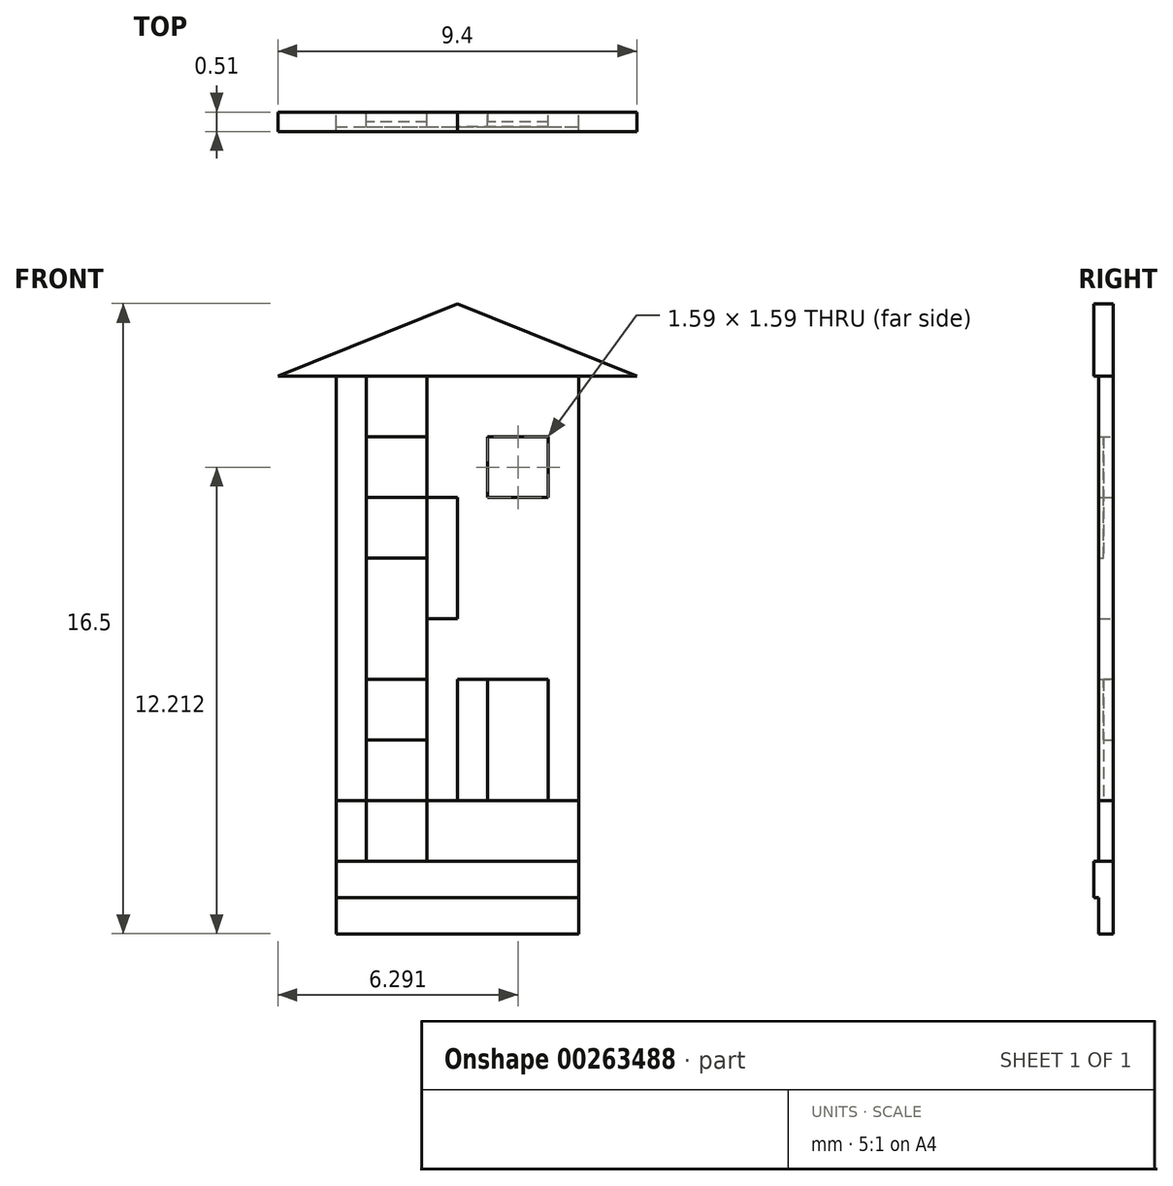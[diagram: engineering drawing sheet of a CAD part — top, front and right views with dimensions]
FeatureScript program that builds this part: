
annotation { "Feature Type Name" : "Feature", "Feature Type Description" : "" }
export const myFeature = defineFeature(function(context is Context, id is Id, definition is map)
    precondition{}
    {
        {
            var Q0;
            Q0=qCreatedBy(makeId("Front.planeOp"),FACE);
            var sketch = newSketch(context, id + "F0", { "sketchPlane" : qUnion([Q0])});
            skLineSegment(sketch, "E0.bottom", {"start": v(-30.22, 33.13) * mm, "end": v(-23.87, 33.13) * mm});
            skLineSegment(sketch, "E0.top", {"start": v(-30.22, 20.43) * mm, "end": v(-23.87, 20.43) * mm});
            skLineSegment(sketch, "E0.left", {"start": v(-30.22, 33.13) * mm, "end": v(-30.22, 20.43) * mm});
            skLineSegment(sketch, "E0.right", {"start": v(-23.87, 33.13) * mm, "end": v(-23.87, 20.43) * mm});
            skLineSegment(sketch, "E1", {"start": v(-27.05, 26.78) * mm, "end": v(-27.05, 20.43) * mm});
            skLineSegment(sketch, "E2", {"start": v(-23.87, 26.78) * mm, "end": v(-30.22, 26.78) * mm});
            skLineSegment(sketch, "E3", {"start": v(-27.05, 33.13) * mm, "end": v(-27.05, 26.78) * mm});
            skLineSegment(sketch, "E4", {"start": v(-28.63, 23.6) * mm, "end": v(-28.63, 20.43) * mm});
            skLineSegment(sketch, "E5", {"start": v(-28.63, 20.43) * mm, "end": v(-28.63, 33.13) * mm});
            skPoint(sketch, "E5.endSnap0", {"position": v(-28.63, 29.96) * mm});
            skLineSegment(sketch, "E6", {"start": v(-25.46, 29.96) * mm, "end": v(-25.46, 33.13) * mm});
            skLineSegment(sketch, "E7", {"start": v(-25.46, 33.13) * mm, "end": v(-25.46, 20.43) * mm});
            skPoint(sketch, "E7.endSnap0", {"position": v(-25.46, 23.6) * mm});
            skLineSegment(sketch, "E8", {"start": v(-28.63, 23.6) * mm, "end": v(-30.22, 23.6) * mm});
            skLineSegment(sketch, "E9", {"start": v(-30.22, 23.6) * mm, "end": v(-23.87, 23.6) * mm});
            skLineSegment(sketch, "E10", {"start": v(-28.63, 29.96) * mm, "end": v(-30.22, 29.96) * mm});
            skLineSegment(sketch, "E11", {"start": v(-30.22, 29.96) * mm, "end": v(-23.87, 29.96) * mm});
            skLineSegment(sketch, "E12", {"start": v(-27.05, 23.6) * mm, "end": v(-27.05, 29.96) * mm});
            skLineSegment(sketch, "E13", {"start": v(-29.43, 31.55) * mm, "end": v(-29.43, 33.13) * mm});
            skLineSegment(sketch, "E14", {"start": v(-29.43, 33.13) * mm, "end": v(-29.43, 20.43) * mm});
            skLineSegment(sketch, "E15", {"start": v(-29.43, 31.55) * mm, "end": v(-30.22, 31.55) * mm});
            skLineSegment(sketch, "E16", {"start": v(-30.22, 31.55) * mm, "end": v(-23.87, 31.55) * mm});
            skLineSegment(sketch, "E17", {"start": v(-27.84, 28.37) * mm, "end": v(-27.84, 33.13) * mm});
            skLineSegment(sketch, "E18", {"start": v(-27.84, 33.13) * mm, "end": v(-27.84, 20.43) * mm});
            skLineSegment(sketch, "E19", {"start": v(-27.84, 28.37) * mm, "end": v(-30.22, 28.37) * mm});
            skLineSegment(sketch, "E20", {"start": v(-30.22, 28.37) * mm, "end": v(-23.87, 28.37) * mm});
            skLineSegment(sketch, "E21", {"start": v(-26.25, 25.2) * mm, "end": v(-26.25, 20.43) * mm});
            skLineSegment(sketch, "E22", {"start": v(-26.25, 20.43) * mm, "end": v(-26.25, 33.13) * mm});
            skLineSegment(sketch, "E23", {"start": v(-26.25, 25.2) * mm, "end": v(-23.87, 25.2) * mm});
            skLineSegment(sketch, "E24", {"start": v(-23.87, 25.2) * mm, "end": v(-30.22, 25.2) * mm});
            skLineSegment(sketch, "E25", {"start": v(-24.67, 22.02) * mm, "end": v(-24.67, 33.13) * mm});
            skLineSegment(sketch, "E26", {"start": v(-24.67, 33.13) * mm, "end": v(-24.67, 20.43) * mm});
            skLineSegment(sketch, "E27", {"start": v(-24.67, 22.02) * mm, "end": v(-23.87, 22.02) * mm});
            skLineSegment(sketch, "E28", {"start": v(-23.87, 22.02) * mm, "end": v(-30.22, 22.02) * mm});
            skPoint(sketch, "E28.endSnap0", {"position": v(-28.63, 22.02) * mm});
            skLineSegment(sketch, "E29", {"start": v(-30.22, 33.13) * mm, "end": v(-31.75, 33.13) * mm});
            skLineSegment(sketch, "E30", {"start": v(-23.87, 33.13) * mm, "end": v(-22.35, 33.13) * mm});
            skLineSegment(sketch, "E31", {"start": v(-27.05, 33.13) * mm, "end": v(-27.05, 35.04) * mm});
            skLineSegment(sketch, "E32", {"start": v(-27.05, 35.04) * mm, "end": v(-31.75, 33.13) * mm});
            skLineSegment(sketch, "E33", {"start": v(-27.05, 35.04) * mm, "end": v(-22.35, 33.13) * mm});
            skLineSegment(sketch, "E34.top", {"start": v(-30.22, 18.54) * mm, "end": v(-23.87, 18.54) * mm});
            skLineSegment(sketch, "E34.left", {"start": v(-30.22, 20.43) * mm, "end": v(-30.22, 18.54) * mm});
            skLineSegment(sketch, "E34.right", {"start": v(-23.87, 20.43) * mm, "end": v(-23.87, 18.54) * mm});
            skLineSegment(sketch, "E35.top", {"start": v(-30.22, 19.48) * mm, "end": v(-23.87, 19.48) * mm});
            skLineSegment(sketch, "E35.left", {"start": v(-30.22, 20.43) * mm, "end": v(-30.22, 19.48) * mm});
            skLineSegment(sketch, "E35.right", {"start": v(-23.87, 20.43) * mm, "end": v(-23.87, 19.48) * mm});
            skSolve(sketch);
        }
        {
            var Q0;
            {var subQ0=sQuery(id+"F0.wireOp",EDGE,"E0.left");var subQ1=sQuery(id+"F0.wireOp",EDGE,"E0.bottom");var subQ2=makeQuery(id+"F0.imprint","INTERSECT",VERTEX,{"derivedFrom":[subQ1,subQ0]});Q0=makeQuery(id+"F0.imprint","IMPRINT",FACE,{"disambiguationData":[TD([[makeQuery(id+"F0.imprint","IMPRINT",EDGE,{"disambiguationData":[TD([[subQ2,-1.0]])],"derivedFrom":subQ1}),-1.0]])]});}
            var Q1;
            {var subQ0=sQuery(id+"F0.wireOp",EDGE,"E11");var subQ1=sQuery(id+"F0.wireOp",EDGE,"E0.left");var subQ2=makeQuery(id+"F0.imprint","INTERSECT",VERTEX,{"derivedFrom":[subQ1,subQ0]});Q1=makeQuery(id+"F0.imprint","IMPRINT",FACE,{"disambiguationData":[TD([[makeQuery(id+"F0.imprint","IMPRINT",EDGE,{"disambiguationData":[TD([[subQ2,1.0]])],"derivedFrom":subQ1}),1.0]])]});}
            var Q2;
            {var subQ0=sQuery(id+"F0.wireOp",EDGE,"E11");var subQ1=sQuery(id+"F0.wireOp",EDGE,"E0.left");var subQ2=makeQuery(id+"F0.imprint","INTERSECT",VERTEX,{"derivedFrom":[subQ1,subQ0]});Q2=makeQuery(id+"F0.imprint","IMPRINT",FACE,{"disambiguationData":[TD([[makeQuery(id+"F0.imprint","IMPRINT",EDGE,{"disambiguationData":[TD([[subQ2,-1.0]])],"derivedFrom":subQ1}),1.0]])]});}
            var Q3;
            {var subQ0=sQuery(id+"F0.wireOp",EDGE,"E2");var subQ1=sQuery(id+"F0.wireOp",EDGE,"E0.left");var subQ2=makeQuery(id+"F0.imprint","INTERSECT",VERTEX,{"derivedFrom":[subQ1,subQ0]});Q3=makeQuery(id+"F0.imprint","IMPRINT",FACE,{"disambiguationData":[TD([[makeQuery(id+"F0.imprint","IMPRINT",EDGE,{"disambiguationData":[TD([[subQ2,1.0]])],"derivedFrom":subQ1}),1.0]])]});}
            var Q4;
            {var subQ0=sQuery(id+"F0.wireOp",EDGE,"E2");var subQ1=sQuery(id+"F0.wireOp",EDGE,"E0.left");var subQ2=makeQuery(id+"F0.imprint","INTERSECT",VERTEX,{"derivedFrom":[subQ1,subQ0]});Q4=makeQuery(id+"F0.imprint","IMPRINT",FACE,{"disambiguationData":[TD([[makeQuery(id+"F0.imprint","IMPRINT",EDGE,{"disambiguationData":[TD([[subQ2,-1.0]])],"derivedFrom":subQ1}),1.0]])]});}
            var Q5;
            {var subQ0=sQuery(id+"F0.wireOp",EDGE,"E9");var subQ1=sQuery(id+"F0.wireOp",EDGE,"E0.left");var subQ2=makeQuery(id+"F0.imprint","INTERSECT",VERTEX,{"derivedFrom":[subQ1,subQ0]});Q5=makeQuery(id+"F0.imprint","IMPRINT",FACE,{"disambiguationData":[TD([[makeQuery(id+"F0.imprint","IMPRINT",EDGE,{"disambiguationData":[TD([[subQ2,1.0]])],"derivedFrom":subQ1}),1.0]])]});}
            var Q6;
            {var subQ0=sQuery(id+"F0.wireOp",EDGE,"E9");var subQ1=sQuery(id+"F0.wireOp",EDGE,"E0.left");var subQ2=makeQuery(id+"F0.imprint","INTERSECT",VERTEX,{"derivedFrom":[subQ1,subQ0]});Q6=makeQuery(id+"F0.imprint","IMPRINT",FACE,{"disambiguationData":[TD([[makeQuery(id+"F0.imprint","IMPRINT",EDGE,{"disambiguationData":[TD([[subQ2,-1.0]])],"derivedFrom":subQ1}),1.0]])]});}
            var Q7;
            {var subQ0=sQuery(id+"F0.wireOp",EDGE,"E0.left");var subQ1=sQuery(id+"F0.wireOp",EDGE,"E0.top");var subQ2=makeQuery(id+"F0.imprint","INTERSECT",VERTEX,{"derivedFrom":[subQ1,subQ0]});Q7=makeQuery(id+"F0.imprint","IMPRINT",FACE,{"disambiguationData":[TD([[makeQuery(id+"F0.imprint","IMPRINT",EDGE,{"disambiguationData":[TD([[subQ2,-1.0]])],"derivedFrom":subQ1}),1.0]])]});}
            var Q8;
            {var subQ0=sQuery(id+"F0.wireOp",EDGE,"E5");var subQ1=sQuery(id+"F0.wireOp",EDGE,"E0.top");var subQ2=makeQuery(id+"F0.imprint","INTERSECT",VERTEX,{"derivedFrom":[subQ1,subQ0]});Q8=makeQuery(id+"F0.imprint","IMPRINT",FACE,{"disambiguationData":[TD([[makeQuery(id+"F0.imprint","IMPRINT",EDGE,{"disambiguationData":[TD([[subQ2,-1.0]])],"derivedFrom":subQ1}),1.0]])]});}
            var Q9;
            {var subQ0=sQuery(id+"F0.wireOp",EDGE,"E5");var subQ1=sQuery(id+"F0.wireOp",EDGE,"E0.top");var subQ2=makeQuery(id+"F0.imprint","INTERSECT",VERTEX,{"derivedFrom":[subQ1,subQ0]});Q9=makeQuery(id+"F0.imprint","IMPRINT",FACE,{"disambiguationData":[TD([[makeQuery(id+"F0.imprint","IMPRINT",EDGE,{"disambiguationData":[TD([[subQ2,1.0]])],"derivedFrom":subQ1}),1.0]])]});}
            var Q10;
            {var subQ0=sQuery(id+"F0.wireOp",EDGE,"E1");var subQ1=sQuery(id+"F0.wireOp",EDGE,"E0.top");var subQ2=makeQuery(id+"F0.imprint","INTERSECT",VERTEX,{"derivedFrom":[subQ1,subQ0]});Q10=makeQuery(id+"F0.imprint","IMPRINT",FACE,{"disambiguationData":[TD([[makeQuery(id+"F0.imprint","IMPRINT",EDGE,{"disambiguationData":[TD([[subQ2,1.0]])],"derivedFrom":subQ1}),1.0]])]});}
            var Q11;
            {var subQ0=sQuery(id+"F0.wireOp",EDGE,"E1");var subQ1=sQuery(id+"F0.wireOp",EDGE,"E0.top");var subQ2=makeQuery(id+"F0.imprint","INTERSECT",VERTEX,{"derivedFrom":[subQ1,subQ0]});Q11=makeQuery(id+"F0.imprint","IMPRINT",FACE,{"disambiguationData":[TD([[makeQuery(id+"F0.imprint","IMPRINT",EDGE,{"disambiguationData":[TD([[subQ2,-1.0]])],"derivedFrom":subQ1}),1.0]])]});}
            var Q12;
            {var subQ0=sQuery(id+"F0.wireOp",EDGE,"E7");var subQ1=sQuery(id+"F0.wireOp",EDGE,"E0.top");var subQ2=makeQuery(id+"F0.imprint","INTERSECT",VERTEX,{"derivedFrom":[subQ1,subQ0]});Q12=makeQuery(id+"F0.imprint","IMPRINT",FACE,{"disambiguationData":[TD([[makeQuery(id+"F0.imprint","IMPRINT",EDGE,{"disambiguationData":[TD([[subQ2,1.0]])],"derivedFrom":subQ1}),1.0]])]});}
            var Q13;
            {var subQ0=sQuery(id+"F0.wireOp",EDGE,"E7");var subQ1=sQuery(id+"F0.wireOp",EDGE,"E0.top");var subQ2=makeQuery(id+"F0.imprint","INTERSECT",VERTEX,{"derivedFrom":[subQ1,subQ0]});Q13=makeQuery(id+"F0.imprint","IMPRINT",FACE,{"disambiguationData":[TD([[makeQuery(id+"F0.imprint","IMPRINT",EDGE,{"disambiguationData":[TD([[subQ2,-1.0]])],"derivedFrom":subQ1}),1.0]])]});}
            var Q14;
            {var subQ0=sQuery(id+"F0.wireOp",EDGE,"E0.right");var subQ1=sQuery(id+"F0.wireOp",EDGE,"E0.top");var subQ2=makeQuery(id+"F0.imprint","INTERSECT",VERTEX,{"derivedFrom":[subQ1,subQ0]});Q14=makeQuery(id+"F0.imprint","IMPRINT",FACE,{"disambiguationData":[TD([[makeQuery(id+"F0.imprint","IMPRINT",EDGE,{"disambiguationData":[TD([[subQ2,1.0]])],"derivedFrom":subQ1}),1.0]])]});}
            var Q15;
            {var subQ0=sQuery(id+"F0.wireOp",EDGE,"E9");var subQ1=sQuery(id+"F0.wireOp",EDGE,"E0.right");var subQ2=makeQuery(id+"F0.imprint","INTERSECT",VERTEX,{"derivedFrom":[subQ1,subQ0]});Q15=makeQuery(id+"F0.imprint","IMPRINT",FACE,{"disambiguationData":[TD([[makeQuery(id+"F0.imprint","IMPRINT",EDGE,{"disambiguationData":[TD([[subQ2,-1.0]])],"derivedFrom":subQ1}),-1.0]])]});}
            var Q16;
            {var subQ0=sQuery(id+"F0.wireOp",EDGE,"E9");var subQ1=sQuery(id+"F0.wireOp",EDGE,"E0.right");var subQ2=makeQuery(id+"F0.imprint","INTERSECT",VERTEX,{"derivedFrom":[subQ1,subQ0]});Q16=makeQuery(id+"F0.imprint","IMPRINT",FACE,{"disambiguationData":[TD([[makeQuery(id+"F0.imprint","IMPRINT",EDGE,{"disambiguationData":[TD([[subQ2,1.0]])],"derivedFrom":subQ1}),-1.0]])]});}
            var Q17;
            {var subQ0=sQuery(id+"F0.wireOp",EDGE,"E2");var subQ1=sQuery(id+"F0.wireOp",EDGE,"E0.right");var subQ2=makeQuery(id+"F0.imprint","INTERSECT",VERTEX,{"derivedFrom":[subQ1,subQ0]});Q17=makeQuery(id+"F0.imprint","IMPRINT",FACE,{"disambiguationData":[TD([[makeQuery(id+"F0.imprint","IMPRINT",EDGE,{"disambiguationData":[TD([[subQ2,-1.0]])],"derivedFrom":subQ1}),-1.0]])]});}
            var Q18;
            {var subQ0=sQuery(id+"F0.wireOp",EDGE,"E2");var subQ1=sQuery(id+"F0.wireOp",EDGE,"E0.right");var subQ2=makeQuery(id+"F0.imprint","INTERSECT",VERTEX,{"derivedFrom":[subQ1,subQ0]});Q18=makeQuery(id+"F0.imprint","IMPRINT",FACE,{"disambiguationData":[TD([[makeQuery(id+"F0.imprint","IMPRINT",EDGE,{"disambiguationData":[TD([[subQ2,1.0]])],"derivedFrom":subQ1}),-1.0]])]});}
            var Q19;
            {var subQ0=sQuery(id+"F0.wireOp",EDGE,"E11");var subQ1=sQuery(id+"F0.wireOp",EDGE,"E0.right");var subQ2=makeQuery(id+"F0.imprint","INTERSECT",VERTEX,{"derivedFrom":[subQ1,subQ0]});Q19=makeQuery(id+"F0.imprint","IMPRINT",FACE,{"disambiguationData":[TD([[makeQuery(id+"F0.imprint","IMPRINT",EDGE,{"disambiguationData":[TD([[subQ2,-1.0]])],"derivedFrom":subQ1}),-1.0]])]});}
            var Q20;
            {var subQ0=sQuery(id+"F0.wireOp",EDGE,"E11");var subQ1=sQuery(id+"F0.wireOp",EDGE,"E0.right");var subQ2=makeQuery(id+"F0.imprint","INTERSECT",VERTEX,{"derivedFrom":[subQ1,subQ0]});Q20=makeQuery(id+"F0.imprint","IMPRINT",FACE,{"disambiguationData":[TD([[makeQuery(id+"F0.imprint","IMPRINT",EDGE,{"disambiguationData":[TD([[subQ2,1.0]])],"derivedFrom":subQ1}),-1.0]])]});}
            var Q21;
            {var subQ0=sQuery(id+"F0.wireOp",EDGE,"E0.right");var subQ1=sQuery(id+"F0.wireOp",EDGE,"E0.bottom");var subQ2=makeQuery(id+"F0.imprint","INTERSECT",VERTEX,{"derivedFrom":[subQ1,subQ0]});Q21=makeQuery(id+"F0.imprint","IMPRINT",FACE,{"disambiguationData":[TD([[makeQuery(id+"F0.imprint","IMPRINT",EDGE,{"disambiguationData":[TD([[subQ2,1.0]])],"derivedFrom":subQ1}),-1.0]])]});}
            var Q22;
            {var subQ0=sQuery(id+"F0.wireOp",EDGE,"E7");var subQ1=sQuery(id+"F0.wireOp",EDGE,"E0.bottom");var subQ2=makeQuery(id+"F0.imprint","INTERSECT",VERTEX,{"derivedFrom":[subQ1,subQ0]});Q22=makeQuery(id+"F0.imprint","IMPRINT",FACE,{"disambiguationData":[TD([[makeQuery(id+"F0.imprint","IMPRINT",EDGE,{"disambiguationData":[TD([[subQ2,-1.0]])],"derivedFrom":subQ1}),-1.0]])]});}
            var Q23;
            {var subQ0=sQuery(id+"F0.wireOp",EDGE,"E7");var subQ1=sQuery(id+"F0.wireOp",EDGE,"E0.bottom");var subQ2=makeQuery(id+"F0.imprint","INTERSECT",VERTEX,{"derivedFrom":[subQ1,subQ0]});Q23=makeQuery(id+"F0.imprint","IMPRINT",FACE,{"disambiguationData":[TD([[makeQuery(id+"F0.imprint","IMPRINT",EDGE,{"disambiguationData":[TD([[subQ2,1.0]])],"derivedFrom":subQ1}),-1.0]])]});}
            var Q24;
            {var subQ0=sQuery(id+"F0.wireOp",EDGE,"E3");var subQ1=sQuery(id+"F0.wireOp",EDGE,"E0.bottom");var subQ2=makeQuery(id+"F0.imprint","INTERSECT",VERTEX,{"derivedFrom":[subQ1,subQ0]});Q24=makeQuery(id+"F0.imprint","IMPRINT",FACE,{"disambiguationData":[TD([[makeQuery(id+"F0.imprint","IMPRINT",EDGE,{"disambiguationData":[TD([[subQ2,-1.0]])],"derivedFrom":subQ1}),-1.0]])]});}
            var Q25;
            {var subQ0=sQuery(id+"F0.wireOp",EDGE,"E3");var subQ1=sQuery(id+"F0.wireOp",EDGE,"E0.bottom");var subQ2=makeQuery(id+"F0.imprint","INTERSECT",VERTEX,{"derivedFrom":[subQ1,subQ0]});Q25=makeQuery(id+"F0.imprint","IMPRINT",FACE,{"disambiguationData":[TD([[makeQuery(id+"F0.imprint","IMPRINT",EDGE,{"disambiguationData":[TD([[subQ2,1.0]])],"derivedFrom":subQ1}),-1.0]])]});}
            var Q26;
            {var subQ0=sQuery(id+"F0.wireOp",EDGE,"E5");var subQ1=sQuery(id+"F0.wireOp",EDGE,"E0.bottom");var subQ2=makeQuery(id+"F0.imprint","INTERSECT",VERTEX,{"derivedFrom":[subQ1,subQ0]});Q26=makeQuery(id+"F0.imprint","IMPRINT",FACE,{"disambiguationData":[TD([[makeQuery(id+"F0.imprint","IMPRINT",EDGE,{"disambiguationData":[TD([[subQ2,-1.0]])],"derivedFrom":subQ1}),-1.0]])]});}
            var Q27;
            {var subQ0=sQuery(id+"F0.wireOp",EDGE,"E5");var subQ1=sQuery(id+"F0.wireOp",EDGE,"E0.bottom");var subQ2=makeQuery(id+"F0.imprint","INTERSECT",VERTEX,{"derivedFrom":[subQ1,subQ0]});Q27=makeQuery(id+"F0.imprint","IMPRINT",FACE,{"disambiguationData":[TD([[makeQuery(id+"F0.imprint","IMPRINT",EDGE,{"disambiguationData":[TD([[subQ2,1.0]])],"derivedFrom":subQ1}),-1.0]])]});}
            var Q28;
            {var subQ1=sQuery(id+"F0.wireOp",EDGE,"E3");var subQ3=sQuery(id+"F0.wireOp",EDGE,"E16");var subQ4=makeQuery(id+"F0.imprint","INTERSECT",VERTEX,{"derivedFrom":[subQ1,subQ3]});Q28=makeQuery(id+"F0.imprint","IMPRINT",FACE,{"disambiguationData":[TD([[makeQuery(id+"F0.imprint","IMPRINT",EDGE,{"disambiguationData":[TD([[subQ4,1.0]])],"derivedFrom":subQ3}),-1.0]])]});}
            var Q29;
            {var subQ1=sQuery(id+"F0.wireOp",EDGE,"E3");var subQ3=sQuery(id+"F0.wireOp",EDGE,"E16");var subQ4=makeQuery(id+"F0.imprint","INTERSECT",VERTEX,{"derivedFrom":[subQ1,subQ3]});Q29=makeQuery(id+"F0.imprint","IMPRINT",FACE,{"disambiguationData":[TD([[makeQuery(id+"F0.imprint","IMPRINT",EDGE,{"disambiguationData":[TD([[subQ4,-1.0]])],"derivedFrom":subQ3}),-1.0]])]});}
            var Q30;
            {var subQ0=sQuery(id+"F0.wireOp",EDGE,"E12");var subQ5=sQuery(id+"F0.wireOp",EDGE,"E20");var subQ6=makeQuery(id+"F0.imprint","INTERSECT",VERTEX,{"derivedFrom":[subQ0,subQ5]});Q30=makeQuery(id+"F0.imprint","IMPRINT",FACE,{"disambiguationData":[TD([[makeQuery(id+"F0.imprint","IMPRINT",EDGE,{"disambiguationData":[TD([[subQ6,-1.0]])],"derivedFrom":subQ5}),1.0]])]});}
            var Q31;
            {var subQ1=sQuery(id+"F0.wireOp",EDGE,"E11");var subQ3=sQuery(id+"F0.wireOp",EDGE,"E18");var subQ4=makeQuery(id+"F0.imprint","INTERSECT",VERTEX,{"derivedFrom":[subQ1,subQ3]});Q31=makeQuery(id+"F0.imprint","IMPRINT",FACE,{"disambiguationData":[TD([[makeQuery(id+"F0.imprint","IMPRINT",EDGE,{"disambiguationData":[TD([[subQ4,-1.0]])],"derivedFrom":subQ3}),1.0]])]});}
            var Q32;
            {var subQ0=sQuery(id+"F0.wireOp",EDGE,"E12");var subQ1=sQuery(id+"F0.wireOp",EDGE,"E2");var subQ2=makeQuery(id+"F0.imprint","INTERSECT",VERTEX,{"derivedFrom":[subQ1,subQ0]});Q32=makeQuery(id+"F0.imprint","IMPRINT",FACE,{"disambiguationData":[TD([[makeQuery(id+"F0.imprint","IMPRINT",EDGE,{"disambiguationData":[TD([[subQ2,-1.0]])],"derivedFrom":subQ1}),-1.0]])]});}
            var Q33;
            {var subQ0=sQuery(id+"F0.wireOp",EDGE,"E22");var subQ1=sQuery(id+"F0.wireOp",EDGE,"E2");var subQ2=makeQuery(id+"F0.imprint","INTERSECT",VERTEX,{"derivedFrom":[subQ1,subQ0]});Q33=makeQuery(id+"F0.imprint","IMPRINT",FACE,{"disambiguationData":[TD([[makeQuery(id+"F0.imprint","IMPRINT",EDGE,{"disambiguationData":[TD([[subQ2,-1.0]])],"derivedFrom":subQ1}),-1.0]])]});}
            var Q34;
            {var subQ0=sQuery(id+"F0.wireOp",EDGE,"E22");var subQ1=sQuery(id+"F0.wireOp",EDGE,"E2");var subQ2=makeQuery(id+"F0.imprint","INTERSECT",VERTEX,{"derivedFrom":[subQ1,subQ0]});Q34=makeQuery(id+"F0.imprint","IMPRINT",FACE,{"disambiguationData":[TD([[makeQuery(id+"F0.imprint","IMPRINT",EDGE,{"disambiguationData":[TD([[subQ2,-1.0]])],"derivedFrom":subQ1}),1.0]])]});}
            var Q35;
            {var subQ0=sQuery(id+"F0.wireOp",EDGE,"E12");var subQ1=sQuery(id+"F0.wireOp",EDGE,"E2");var subQ2=makeQuery(id+"F0.imprint","INTERSECT",VERTEX,{"derivedFrom":[subQ1,subQ0]});Q35=makeQuery(id+"F0.imprint","IMPRINT",FACE,{"disambiguationData":[TD([[makeQuery(id+"F0.imprint","IMPRINT",EDGE,{"disambiguationData":[TD([[subQ2,-1.0]])],"derivedFrom":subQ1}),1.0]])]});}
            var Q36;
            {var subQ1=sQuery(id+"F0.wireOp",EDGE,"E9");var subQ3=sQuery(id+"F0.wireOp",EDGE,"E22");var subQ4=makeQuery(id+"F0.imprint","INTERSECT",VERTEX,{"derivedFrom":[subQ1,subQ3]});Q36=makeQuery(id+"F0.imprint","IMPRINT",FACE,{"disambiguationData":[TD([[makeQuery(id+"F0.imprint","IMPRINT",EDGE,{"disambiguationData":[TD([[subQ4,-1.0]])],"derivedFrom":subQ3}),1.0]])]});}
            var Q37;
            {var subQ1=sQuery(id+"F0.wireOp",EDGE,"E9");var subQ3=sQuery(id+"F0.wireOp",EDGE,"E18");var subQ4=makeQuery(id+"F0.imprint","INTERSECT",VERTEX,{"derivedFrom":[subQ1,subQ3]});Q37=makeQuery(id+"F0.imprint","IMPRINT",FACE,{"disambiguationData":[TD([[makeQuery(id+"F0.imprint","IMPRINT",EDGE,{"disambiguationData":[TD([[subQ4,1.0]])],"derivedFrom":subQ3}),1.0]])]});}
            var Q38;
            {var subQ0=sQuery(id+"F0.wireOp",EDGE,"E9");var subQ5=sQuery(id+"F0.wireOp",EDGE,"E18");var subQ6=makeQuery(id+"F0.imprint","INTERSECT",VERTEX,{"derivedFrom":[subQ0,subQ5]});Q38=makeQuery(id+"F0.imprint","IMPRINT",FACE,{"disambiguationData":[TD([[makeQuery(id+"F0.imprint","IMPRINT",EDGE,{"disambiguationData":[TD([[subQ6,-1.0]])],"derivedFrom":subQ5}),1.0]])]});}
            var Q39;
            {var subQ0=sQuery(id+"F0.wireOp",EDGE,"E9");var subQ5=sQuery(id+"F0.wireOp",EDGE,"E22");var subQ6=makeQuery(id+"F0.imprint","INTERSECT",VERTEX,{"derivedFrom":[subQ0,subQ5]});Q39=makeQuery(id+"F0.imprint","IMPRINT",FACE,{"disambiguationData":[TD([[makeQuery(id+"F0.imprint","IMPRINT",EDGE,{"disambiguationData":[TD([[subQ6,1.0]])],"derivedFrom":subQ5}),1.0]])]});}
            var Q40;
            {var subQ0=sQuery(id+"F0.wireOp",EDGE,"E18");var subQ1=sQuery(id+"F0.wireOp",EDGE,"E2");var subQ2=makeQuery(id+"F0.imprint","INTERSECT",VERTEX,{"derivedFrom":[subQ1,subQ0]});Q40=makeQuery(id+"F0.imprint","IMPRINT",FACE,{"disambiguationData":[TD([[makeQuery(id+"F0.imprint","IMPRINT",EDGE,{"disambiguationData":[TD([[subQ2,-1.0]])],"derivedFrom":subQ1}),-1.0]])]});}
            var Q41;
            {var subQ0=sQuery(id+"F0.wireOp",EDGE,"E5");var subQ1=sQuery(id+"F0.wireOp",EDGE,"E2");var subQ2=makeQuery(id+"F0.imprint","INTERSECT",VERTEX,{"derivedFrom":[subQ1,subQ0]});Q41=makeQuery(id+"F0.imprint","IMPRINT",FACE,{"disambiguationData":[TD([[makeQuery(id+"F0.imprint","IMPRINT",EDGE,{"disambiguationData":[TD([[subQ2,-1.0]])],"derivedFrom":subQ1}),-1.0]])]});}
            var Q42;
            {var subQ0=sQuery(id+"F0.wireOp",EDGE,"E5");var subQ1=sQuery(id+"F0.wireOp",EDGE,"E2");var subQ2=makeQuery(id+"F0.imprint","INTERSECT",VERTEX,{"derivedFrom":[subQ1,subQ0]});Q42=makeQuery(id+"F0.imprint","IMPRINT",FACE,{"disambiguationData":[TD([[makeQuery(id+"F0.imprint","IMPRINT",EDGE,{"disambiguationData":[TD([[subQ2,-1.0]])],"derivedFrom":subQ1}),1.0]])]});}
            var Q43;
            {var subQ0=sQuery(id+"F0.wireOp",EDGE,"E18");var subQ1=sQuery(id+"F0.wireOp",EDGE,"E2");var subQ2=makeQuery(id+"F0.imprint","INTERSECT",VERTEX,{"derivedFrom":[subQ1,subQ0]});Q43=makeQuery(id+"F0.imprint","IMPRINT",FACE,{"disambiguationData":[TD([[makeQuery(id+"F0.imprint","IMPRINT",EDGE,{"disambiguationData":[TD([[subQ2,-1.0]])],"derivedFrom":subQ1}),1.0]])]});}
            var Q44;
            {var subQ0=sQuery(id+"F0.wireOp",EDGE,"E7");var subQ1=sQuery(id+"F0.wireOp",EDGE,"E2");var subQ2=makeQuery(id+"F0.imprint","INTERSECT",VERTEX,{"derivedFrom":[subQ1,subQ0]});Q44=makeQuery(id+"F0.imprint","IMPRINT",FACE,{"disambiguationData":[TD([[makeQuery(id+"F0.imprint","IMPRINT",EDGE,{"disambiguationData":[TD([[subQ2,-1.0]])],"derivedFrom":subQ1}),-1.0]])]});}
            var Q45;
            {var subQ0=sQuery(id+"F0.wireOp",EDGE,"E7");var subQ1=sQuery(id+"F0.wireOp",EDGE,"E2");var subQ2=makeQuery(id+"F0.imprint","INTERSECT",VERTEX,{"derivedFrom":[subQ1,subQ0]});Q45=makeQuery(id+"F0.imprint","IMPRINT",FACE,{"disambiguationData":[TD([[makeQuery(id+"F0.imprint","IMPRINT",EDGE,{"disambiguationData":[TD([[subQ2,-1.0]])],"derivedFrom":subQ1}),1.0]])]});}
            var Q46;
            {var subQ0=sQuery(id+"F0.wireOp",EDGE,"E26");var subQ1=sQuery(id+"F0.wireOp",EDGE,"E2");var subQ2=makeQuery(id+"F0.imprint","INTERSECT",VERTEX,{"derivedFrom":[subQ1,subQ0]});Q46=makeQuery(id+"F0.imprint","IMPRINT",FACE,{"disambiguationData":[TD([[makeQuery(id+"F0.imprint","IMPRINT",EDGE,{"disambiguationData":[TD([[subQ2,-1.0]])],"derivedFrom":subQ1}),1.0]])]});}
            var Q47;
            {var subQ0=sQuery(id+"F0.wireOp",EDGE,"E26");var subQ1=sQuery(id+"F0.wireOp",EDGE,"E2");var subQ2=makeQuery(id+"F0.imprint","INTERSECT",VERTEX,{"derivedFrom":[subQ1,subQ0]});Q47=makeQuery(id+"F0.imprint","IMPRINT",FACE,{"disambiguationData":[TD([[makeQuery(id+"F0.imprint","IMPRINT",EDGE,{"disambiguationData":[TD([[subQ2,-1.0]])],"derivedFrom":subQ1}),-1.0]])]});}
            extrude(context, id + "F1", {"entities" : qUnion([Q0, Q1, Q2, Q3, Q4, Q5, Q6, Q7, Q8, Q9, Q10, Q11, Q12, Q13, Q14, Q15, Q16, Q17, Q18, Q19, Q20, Q21, Q22, Q23, Q24, Q25, Q26, Q27, Q28, Q29, Q30, Q31, Q32, Q33, Q34, Q35, Q36, Q37, Q38, Q39, Q40, Q41, Q42, Q43, Q44, Q45, Q46, Q47]), "depth" : 0.38 * mm});
        }
        {
            var Q0;
            {var subQ0=sQuery(id+"F0.wireOp",EDGE,"E11");var subQ1=sQuery(id+"F0.wireOp",EDGE,"E5");var subQ2=makeQuery(id+"F0.imprint","INTERSECT",VERTEX,{"derivedFrom":[subQ1,subQ0]});Q0=makeQuery(id+"F0.imprint","IMPRINT",FACE,{"disambiguationData":[TD([[makeQuery(id+"F0.imprint","IMPRINT",EDGE,{"disambiguationData":[TD([[subQ2,-1.0]])],"derivedFrom":subQ1}),1.0]])]});}
            var Q1;
            {var subQ0=sQuery(id+"F0.wireOp",EDGE,"E11");var subQ1=sQuery(id+"F0.wireOp",EDGE,"E5");var subQ2=makeQuery(id+"F0.imprint","INTERSECT",VERTEX,{"derivedFrom":[subQ1,subQ0]});Q1=makeQuery(id+"F0.imprint","IMPRINT",FACE,{"disambiguationData":[TD([[makeQuery(id+"F0.imprint","IMPRINT",EDGE,{"disambiguationData":[TD([[subQ2,-1.0]])],"derivedFrom":subQ1}),-1.0]])]});}
            var Q2;
            {var subQ0=sQuery(id+"F0.wireOp",EDGE,"E20");var subQ1=sQuery(id+"F0.wireOp",EDGE,"E5");var subQ2=makeQuery(id+"F0.imprint","INTERSECT",VERTEX,{"derivedFrom":[subQ1,subQ0]});Q2=makeQuery(id+"F0.imprint","IMPRINT",FACE,{"disambiguationData":[TD([[makeQuery(id+"F0.imprint","IMPRINT",EDGE,{"disambiguationData":[TD([[subQ2,-1.0]])],"derivedFrom":subQ1}),-1.0]])]});}
            var Q3;
            {var subQ0=sQuery(id+"F0.wireOp",EDGE,"E20");var subQ1=sQuery(id+"F0.wireOp",EDGE,"E5");var subQ2=makeQuery(id+"F0.imprint","INTERSECT",VERTEX,{"derivedFrom":[subQ1,subQ0]});Q3=makeQuery(id+"F0.imprint","IMPRINT",FACE,{"disambiguationData":[TD([[makeQuery(id+"F0.imprint","IMPRINT",EDGE,{"disambiguationData":[TD([[subQ2,-1.0]])],"derivedFrom":subQ1}),1.0]])]});}
            var Q4;
            {var subQ0=sQuery(id+"F0.wireOp",EDGE,"E16");var subQ1=sQuery(id+"F0.wireOp",EDGE,"E7");var subQ2=makeQuery(id+"F0.imprint","INTERSECT",VERTEX,{"derivedFrom":[subQ1,subQ0]});Q4=makeQuery(id+"F0.imprint","IMPRINT",FACE,{"disambiguationData":[TD([[makeQuery(id+"F0.imprint","IMPRINT",EDGE,{"disambiguationData":[TD([[subQ2,-1.0]])],"derivedFrom":subQ1}),-1.0]])]});}
            var Q5;
            {var subQ0=sQuery(id+"F0.wireOp",EDGE,"E11");var subQ1=sQuery(id+"F0.wireOp",EDGE,"E7");var subQ2=makeQuery(id+"F0.imprint","INTERSECT",VERTEX,{"derivedFrom":[subQ1,subQ0]});Q5=makeQuery(id+"F0.imprint","IMPRINT",FACE,{"disambiguationData":[TD([[makeQuery(id+"F0.imprint","IMPRINT",EDGE,{"disambiguationData":[TD([[subQ2,-1.0]])],"derivedFrom":subQ1}),-1.0]])]});}
            var Q6;
            {var subQ0=sQuery(id+"F0.wireOp",EDGE,"E16");var subQ1=sQuery(id+"F0.wireOp",EDGE,"E7");var subQ2=makeQuery(id+"F0.imprint","INTERSECT",VERTEX,{"derivedFrom":[subQ1,subQ0]});Q6=makeQuery(id+"F0.imprint","IMPRINT",FACE,{"disambiguationData":[TD([[makeQuery(id+"F0.imprint","IMPRINT",EDGE,{"disambiguationData":[TD([[subQ2,-1.0]])],"derivedFrom":subQ1}),1.0]])]});}
            var Q7;
            {var subQ0=sQuery(id+"F0.wireOp",EDGE,"E11");var subQ1=sQuery(id+"F0.wireOp",EDGE,"E7");var subQ2=makeQuery(id+"F0.imprint","INTERSECT",VERTEX,{"derivedFrom":[subQ1,subQ0]});Q7=makeQuery(id+"F0.imprint","IMPRINT",FACE,{"disambiguationData":[TD([[makeQuery(id+"F0.imprint","IMPRINT",EDGE,{"disambiguationData":[TD([[subQ2,-1.0]])],"derivedFrom":subQ1}),1.0]])]});}
            var Q8;
            {var subQ0=sQuery(id+"F0.wireOp",EDGE,"E9");var subQ1=sQuery(id+"F0.wireOp",EDGE,"E5");var subQ2=makeQuery(id+"F0.imprint","INTERSECT",VERTEX,{"derivedFrom":[subQ1,subQ0]});Q8=makeQuery(id+"F0.imprint","IMPRINT",FACE,{"disambiguationData":[TD([[makeQuery(id+"F0.imprint","IMPRINT",EDGE,{"disambiguationData":[TD([[subQ2,-1.0]])],"derivedFrom":subQ1}),1.0]])]});}
            var Q9;
            {var subQ0=sQuery(id+"F0.wireOp",EDGE,"E9");var subQ1=sQuery(id+"F0.wireOp",EDGE,"E5");var subQ2=makeQuery(id+"F0.imprint","INTERSECT",VERTEX,{"derivedFrom":[subQ1,subQ0]});Q9=makeQuery(id+"F0.imprint","IMPRINT",FACE,{"disambiguationData":[TD([[makeQuery(id+"F0.imprint","IMPRINT",EDGE,{"disambiguationData":[TD([[subQ2,-1.0]])],"derivedFrom":subQ1}),-1.0]])]});}
            var Q10;
            {var subQ0=sQuery(id+"F0.wireOp",EDGE,"E28");var subQ1=sQuery(id+"F0.wireOp",EDGE,"E5");var subQ2=makeQuery(id+"F0.imprint","INTERSECT",VERTEX,{"derivedFrom":[subQ1,subQ0]});Q10=makeQuery(id+"F0.imprint","IMPRINT",FACE,{"disambiguationData":[TD([[makeQuery(id+"F0.imprint","IMPRINT",EDGE,{"disambiguationData":[TD([[subQ2,-1.0]])],"derivedFrom":subQ1}),-1.0]])]});}
            var Q11;
            {var subQ0=sQuery(id+"F0.wireOp",EDGE,"E28");var subQ1=sQuery(id+"F0.wireOp",EDGE,"E5");var subQ2=makeQuery(id+"F0.imprint","INTERSECT",VERTEX,{"derivedFrom":[subQ1,subQ0]});Q11=makeQuery(id+"F0.imprint","IMPRINT",FACE,{"disambiguationData":[TD([[makeQuery(id+"F0.imprint","IMPRINT",EDGE,{"disambiguationData":[TD([[subQ2,-1.0]])],"derivedFrom":subQ1}),1.0]])]});}
            var Q12;
            {var subQ0=sQuery(id+"F0.wireOp",EDGE,"E9");var subQ1=sQuery(id+"F0.wireOp",EDGE,"E7");var subQ2=makeQuery(id+"F0.imprint","INTERSECT",VERTEX,{"derivedFrom":[subQ1,subQ0]});Q12=makeQuery(id+"F0.imprint","IMPRINT",FACE,{"disambiguationData":[TD([[makeQuery(id+"F0.imprint","IMPRINT",EDGE,{"disambiguationData":[TD([[subQ2,-1.0]])],"derivedFrom":subQ1}),-1.0]])]});}
            var Q13;
            {var subQ0=sQuery(id+"F0.wireOp",EDGE,"E9");var subQ1=sQuery(id+"F0.wireOp",EDGE,"E7");var subQ2=makeQuery(id+"F0.imprint","INTERSECT",VERTEX,{"derivedFrom":[subQ1,subQ0]});Q13=makeQuery(id+"F0.imprint","IMPRINT",FACE,{"disambiguationData":[TD([[makeQuery(id+"F0.imprint","IMPRINT",EDGE,{"disambiguationData":[TD([[subQ2,-1.0]])],"derivedFrom":subQ1}),1.0]])]});}
            var Q14;
            {var subQ0=sQuery(id+"F0.wireOp",EDGE,"E24");var subQ1=sQuery(id+"F0.wireOp",EDGE,"E7");var subQ2=makeQuery(id+"F0.imprint","INTERSECT",VERTEX,{"derivedFrom":[subQ1,subQ0]});Q14=makeQuery(id+"F0.imprint","IMPRINT",FACE,{"disambiguationData":[TD([[makeQuery(id+"F0.imprint","IMPRINT",EDGE,{"disambiguationData":[TD([[subQ2,-1.0]])],"derivedFrom":subQ1}),1.0]])]});}
            var Q15;
            {var subQ0=sQuery(id+"F0.wireOp",EDGE,"E24");var subQ1=sQuery(id+"F0.wireOp",EDGE,"E7");var subQ2=makeQuery(id+"F0.imprint","INTERSECT",VERTEX,{"derivedFrom":[subQ1,subQ0]});Q15=makeQuery(id+"F0.imprint","IMPRINT",FACE,{"disambiguationData":[TD([[makeQuery(id+"F0.imprint","IMPRINT",EDGE,{"disambiguationData":[TD([[subQ2,-1.0]])],"derivedFrom":subQ1}),-1.0]])]});}
            extrude(context, id + "F2", {"entities" : qUnion([Q0, Q1, Q2, Q3, Q4, Q5, Q6, Q7, Q8, Q9, Q10, Q11, Q12, Q13, Q14, Q15]), "operationType" : NewBodyOperationType.ADD, "depth" : 0.25 * mm});
        }
        {
            var Q0;
            {var subQ5=sQuery(id+"F0.wireOp",EDGE,"E29");Q0=makeQuery(id+"F0.imprint","IMPRINT",FACE,{"disambiguationData":[TD([[makeQuery(id+"F0.imprint","IMPRINT",EDGE,{"derivedFrom":subQ5}),-1.0]])]});}
            var Q1;
            {var subQ0=sQuery(id+"F0.wireOp",EDGE,"E30");Q1=makeQuery(id+"F0.imprint","IMPRINT",FACE,{"disambiguationData":[TD([[makeQuery(id+"F0.imprint","IMPRINT",EDGE,{"derivedFrom":subQ0}),1.0]])]});}
            extrude(context, id + "F3", {"entities" : qUnion([Q0, Q1]), "operationType" : NewBodyOperationType.ADD, "depth" : 0.5 * mm});
        }
        {
            var Q0;
            Q0=makeQuery(id+"F0.imprint","IMPRINT",FACE,{"disambiguationData":[TD([[makeQuery(id+"F0.imprint","IMPRINT",EDGE,{"derivedFrom":sQuery(id+"F0.wireOp",EDGE,"E35.top")}),1.0]])]});
            extrude(context, id + "F4", {"entities" : qUnion([Q0]), "depth" : 0.5 * mm});
        }
        {
            var Q0;
            {var subQ0=sQuery(id+"F0.wireOp",EDGE,"E0.top");var subQ5=sQuery(id+"F0.wireOp",EDGE,"E14");var subQ6=makeQuery(id+"F0.imprint","INTERSECT",VERTEX,{"derivedFrom":[subQ5,subQ0]});Q0=makeQuery(id+"F0.imprint","IMPRINT",FACE,{"disambiguationData":[TD([[makeQuery(id+"F0.imprint","IMPRINT",EDGE,{"disambiguationData":[TD([[subQ6,1.0]])],"derivedFrom":subQ5}),-1.0]])]});}
            var Q1;
            {var subQ0=sQuery(id+"F0.wireOp",EDGE,"E0.top");var subQ1=sQuery(id+"F0.wireOp",EDGE,"E5");var subQ2=makeQuery(id+"F0.imprint","INTERSECT",VERTEX,{"derivedFrom":[subQ1,subQ0]});Q1=makeQuery(id+"F0.imprint","IMPRINT",FACE,{"disambiguationData":[TD([[makeQuery(id+"F0.imprint","IMPRINT",EDGE,{"disambiguationData":[TD([[subQ2,-1.0]])],"derivedFrom":subQ1}),1.0]])]});}
            var Q2;
            {var subQ0=sQuery(id+"F0.wireOp",EDGE,"E0.top");var subQ1=sQuery(id+"F0.wireOp",EDGE,"E5");var subQ2=makeQuery(id+"F0.imprint","INTERSECT",VERTEX,{"derivedFrom":[subQ1,subQ0]});Q2=makeQuery(id+"F0.imprint","IMPRINT",FACE,{"disambiguationData":[TD([[makeQuery(id+"F0.imprint","IMPRINT",EDGE,{"disambiguationData":[TD([[subQ2,-1.0]])],"derivedFrom":subQ1}),-1.0]])]});}
            var Q3;
            {var subQ0=sQuery(id+"F0.wireOp",EDGE,"E0.top");var subQ1=sQuery(id+"F0.wireOp",EDGE,"E1");var subQ2=makeQuery(id+"F0.imprint","INTERSECT",VERTEX,{"derivedFrom":[subQ1,subQ0]});Q3=makeQuery(id+"F0.imprint","IMPRINT",FACE,{"disambiguationData":[TD([[makeQuery(id+"F0.imprint","IMPRINT",EDGE,{"disambiguationData":[TD([[subQ2,1.0]])],"derivedFrom":subQ1}),-1.0]])]});}
            var Q4;
            {var subQ0=sQuery(id+"F0.wireOp",EDGE,"E0.top");var subQ1=sQuery(id+"F0.wireOp",EDGE,"E1");var subQ2=makeQuery(id+"F0.imprint","INTERSECT",VERTEX,{"derivedFrom":[subQ1,subQ0]});Q4=makeQuery(id+"F0.imprint","IMPRINT",FACE,{"disambiguationData":[TD([[makeQuery(id+"F0.imprint","IMPRINT",EDGE,{"disambiguationData":[TD([[subQ2,1.0]])],"derivedFrom":subQ1}),1.0]])]});}
            var Q5;
            {var subQ0=sQuery(id+"F0.wireOp",EDGE,"E0.top");var subQ1=sQuery(id+"F0.wireOp",EDGE,"E7");var subQ2=makeQuery(id+"F0.imprint","INTERSECT",VERTEX,{"derivedFrom":[subQ1,subQ0]});Q5=makeQuery(id+"F0.imprint","IMPRINT",FACE,{"disambiguationData":[TD([[makeQuery(id+"F0.imprint","IMPRINT",EDGE,{"disambiguationData":[TD([[subQ2,1.0]])],"derivedFrom":subQ1}),-1.0]])]});}
            var Q6;
            {var subQ0=sQuery(id+"F0.wireOp",EDGE,"E0.top");var subQ1=sQuery(id+"F0.wireOp",EDGE,"E7");var subQ2=makeQuery(id+"F0.imprint","INTERSECT",VERTEX,{"derivedFrom":[subQ1,subQ0]});Q6=makeQuery(id+"F0.imprint","IMPRINT",FACE,{"disambiguationData":[TD([[makeQuery(id+"F0.imprint","IMPRINT",EDGE,{"disambiguationData":[TD([[subQ2,1.0]])],"derivedFrom":subQ1}),1.0]])]});}
            var Q7;
            {var subQ0=sQuery(id+"F0.wireOp",EDGE,"E0.top");var subQ5=sQuery(id+"F0.wireOp",EDGE,"E26");var subQ7=makeQuery(id+"F0.imprint","INTERSECT",VERTEX,{"derivedFrom":[subQ5,subQ0]});Q7=makeQuery(id+"F0.imprint","IMPRINT",FACE,{"disambiguationData":[TD([[makeQuery(id+"F0.imprint","IMPRINT",EDGE,{"disambiguationData":[TD([[subQ7,1.0]])],"derivedFrom":subQ5}),1.0]])]});}
            extrude(context, id + "F5", {"entities" : qUnion([Q0, Q1, Q2, Q3, Q4, Q5, Q6, Q7]), "depth" : 0.38 * mm});
        }
        {
            var Q0;
            Q0=makeQuery(id+"F0.imprint","IMPRINT",FACE,{"disambiguationData":[TD([[makeQuery(id+"F0.imprint","IMPRINT",EDGE,{"derivedFrom":sQuery(id+"F0.wireOp",EDGE,"E34.top")}),1.0]])]});
            extrude(context, id + "F6", {"entities" : qUnion([Q0]), "operationType" : NewBodyOperationType.ADD, "depth" : 0.38 * mm});
        }
    });
